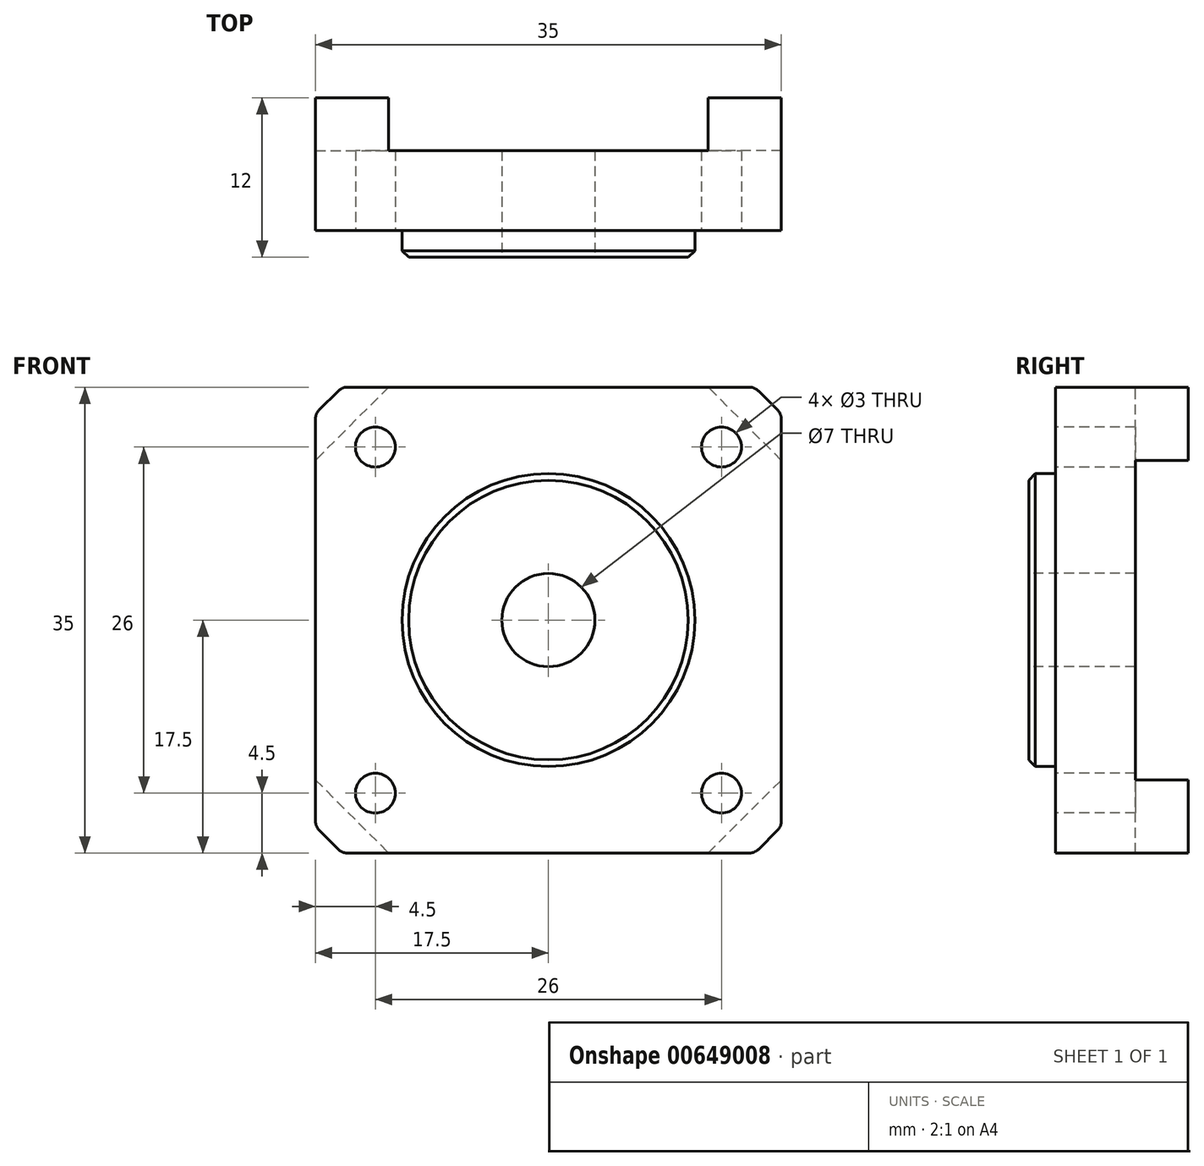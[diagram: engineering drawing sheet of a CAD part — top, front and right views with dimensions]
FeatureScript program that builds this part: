
annotation { "Feature Type Name" : "Feature", "Feature Type Description" : "" }
export const myFeature = defineFeature(function(context is Context, id is Id, definition is map)
    precondition{}
    {
        {
            var Q0;
            Q0=qCreatedBy(makeId("Front.planeOp"),FACE);
            var sketch = newSketch(context, id + "F0", { "sketchPlane" : qUnion([Q0])});
            skLineSegment(sketch, "E0.bottom", {"start": v(-17.5, 17.5) * mm, "end": v(17.5, 17.5) * mm});
            skLineSegment(sketch, "E0.top", {"start": v(-17.5, -17.5) * mm, "end": v(17.5, -17.5) * mm});
            skLineSegment(sketch, "E0.left", {"start": v(-17.5, 17.5) * mm, "end": v(-17.5, -17.5) * mm});
            skLineSegment(sketch, "E0.right", {"start": v(17.5, 17.5) * mm, "end": v(17.5, -17.5) * mm});
            skPoint(sketch, "E0.middle", {"position": v(0, 0) * mm});
            skSolve(sketch);
        }
        {
            var Q0;
            Q0=makeQuery(id+"F0.imprint","IMPRINT",FACE,{"disambiguationData":[TD([[makeQuery(id+"F0.imprint","IMPRINT",EDGE,{"derivedFrom":sQuery(id+"F0.wireOp",EDGE,"E0.bottom")}),-1.0]])]});
            extrude(context, id + "F1", {"entities" : qUnion([Q0]), "depth" : 10 * mm, "offsetDistance" : 25 * mm});
        }
        {
            var Q0;
            Q0=makeQuery(id+"F1.opExtrude","SWEPT_EDGE",EDGE,{"disambiguationData":[OSD([sQuery(id+"F0.wireOp",EDGE,"E0.bottom"),sQuery(id+"F0.wireOp",EDGE,"E0.left")])]});
            var Q1;
            Q1=makeQuery(id+"F1.opExtrude","SWEPT_EDGE",EDGE,{"disambiguationData":[OSD([sQuery(id+"F0.wireOp",EDGE,"E0.bottom"),sQuery(id+"F0.wireOp",EDGE,"E0.right")])]});
            var Q2;
            Q2=makeQuery(id+"F1.opExtrude","SWEPT_EDGE",EDGE,{"disambiguationData":[OSD([sQuery(id+"F0.wireOp",EDGE,"E0.top"),sQuery(id+"F0.wireOp",EDGE,"E0.right")])]});
            var Q3;
            Q3=makeQuery(id+"F1.opExtrude","SWEPT_EDGE",EDGE,{"disambiguationData":[OSD([sQuery(id+"F0.wireOp",EDGE,"E0.top"),sQuery(id+"F0.wireOp",EDGE,"E0.left")])]});
            chamfer(context, id + "F2", {"entities" : qUnion([Q0, Q1, Q2, Q3]), "width" : 2 * mm, "tangentPropagation" : true});
        }
        {
            var Q0;
            Q0=makeQuery(id+"F1.opExtrude","CAP_FACE",FACE,{"disambiguationData":[OSD([sQuery(id+"F0.wireOp",EDGE,"E0.bottom"),sQuery(id+"F0.wireOp",EDGE,"E0.top"),sQuery(id+"F0.wireOp",EDGE,"E0.left"),sQuery(id+"F0.wireOp",EDGE,"E0.right")])],"isStart":false});
            var sketch = newSketch(context, id + "F3", { "sketchPlane" : qUnion([Q0])});
            skCircle(sketch, "E1", {"center": v(0, 0) * mm, "radius": 11 * mm});
            skSolve(sketch);
        }
        {
            var Q0;
            Q0=makeQuery(id+"F3.imprint","IMPRINT",FACE,{"disambiguationData":[TD([[makeQuery(id+"F3.imprint","IMPRINT",EDGE,{"derivedFrom":sQuery(id+"F3.wireOp",EDGE,"E1")}),1.0]])]});
            extrude(context, id + "F4", {"entities" : qUnion([Q0]), "operationType" : NewBodyOperationType.REMOVE, "oppositeDirection" : true, "depth" : 0.5 * mm, "offsetDistance" : 25 * mm});
        }
        {
            var Q0;
            Q0=makeQuery(id+"F4.boolean.opBoolean","COPY",FACE,{"derivedFrom":makeQuery(id+"F4.opExtrude","CAP_FACE",FACE,{"disambiguationData":[OSD([sQuery(id+"F3.wireOp",EDGE,"E1")])],"isStart":false})});
            var sketch = newSketch(context, id + "F5", { "sketchPlane" : qUnion([Q0])});
            skCircle(sketch, "E2", {"center": v(0, 0) * mm, "radius": 11 * mm});
            skSolve(sketch);
        }
        {
            var Q0;
            Q0=makeQuery(id+"F5.imprint","IMPRINT",FACE,{"disambiguationData":[TD([[makeQuery(id+"F5.imprint","IMPRINT",EDGE,{"derivedFrom":sQuery(id+"F5.wireOp",EDGE,"E2")}),1.0]])]});
            extrude(context, id + "F6", {"entities" : qUnion([Q0]), "operationType" : NewBodyOperationType.ADD, "depth" : 2.5 * mm, "offsetDistance" : 25 * mm});
        }
        {
            var Q0;
            Q0=makeQuery(id+"F6.opExtrude","CAP_FACE",FACE,{"disambiguationData":[OSD([sQuery(id+"F5.wireOp",EDGE,"E2")])],"isStart":false});
            var sketch = newSketch(context, id + "F7", { "sketchPlane" : qUnion([Q0])});
            skCircle(sketch, "E3", {"center": v(0, 0) * mm, "radius": 3.5 * mm});
            skSolve(sketch);
        }
        {
            var Q0;
            Q0=makeQuery(id+"F7.imprint","IMPRINT",FACE,{"disambiguationData":[TD([[makeQuery(id+"F7.imprint","IMPRINT",EDGE,{"derivedFrom":sQuery(id+"F7.wireOp",EDGE,"E3")}),1.0]])]});
            var Q1;
            Q1=sQuery(id+"F7.wireOp",EDGE,"E3");
            extrude(context, id + "F8", {"entities" : qUnion([Q0]), "operationType" : NewBodyOperationType.REMOVE, "surfaceEntities" : qUnion([Q1]), "endBound" : BoundingType.THROUGH_ALL, "oppositeDirection" : true, "depth" : 25 * mm, "offsetDistance" : 25 * mm});
        }
        {
            var Q0;
            {var subQ0=sQuery(id+"F0.wireOp",EDGE,"E0.bottom");Q0=makeQuery(id+"F2.opChamfer","BLEND_EDGE",EDGE,{"blendedFrom":[makeQuery(id+"F1.opExtrude","SWEPT_EDGE",EDGE,{"disambiguationData":[OSD([subQ0,sQuery(id+"F0.wireOp",EDGE,"E0.left")])]}),makeQuery(id+"F1.opExtrude","SWEPT_FACE",FACE,{"disambiguationData":[OSD([subQ0])]})],"blendedInto":[makeQuery(id+"F1.opExtrude","SWEPT_FACE",FACE,{"disambiguationData":[OSD([subQ0])]})]});}
            var Q1;
            {var subQ0=sQuery(id+"F0.wireOp",EDGE,"E0.bottom");Q1=makeQuery(id+"F2.opChamfer","BLEND_EDGE",EDGE,{"blendedFrom":[makeQuery(id+"F1.opExtrude","SWEPT_EDGE",EDGE,{"disambiguationData":[OSD([subQ0,sQuery(id+"F0.wireOp",EDGE,"E0.right")])]}),makeQuery(id+"F1.opExtrude","SWEPT_FACE",FACE,{"disambiguationData":[OSD([subQ0])]})],"blendedInto":[makeQuery(id+"F1.opExtrude","SWEPT_FACE",FACE,{"disambiguationData":[OSD([subQ0])]})]});}
            var Q2;
            {var subQ0=sQuery(id+"F0.wireOp",EDGE,"E0.right");Q2=makeQuery(id+"F2.opChamfer","BLEND_EDGE",EDGE,{"blendedFrom":[makeQuery(id+"F1.opExtrude","SWEPT_EDGE",EDGE,{"disambiguationData":[OSD([sQuery(id+"F0.wireOp",EDGE,"E0.bottom"),subQ0])]}),makeQuery(id+"F1.opExtrude","SWEPT_FACE",FACE,{"disambiguationData":[OSD([subQ0])]})],"blendedInto":[makeQuery(id+"F1.opExtrude","SWEPT_FACE",FACE,{"disambiguationData":[OSD([subQ0])]})]});}
            var Q3;
            {var subQ0=sQuery(id+"F0.wireOp",EDGE,"E0.right");Q3=makeQuery(id+"F2.opChamfer","BLEND_EDGE",EDGE,{"blendedFrom":[makeQuery(id+"F1.opExtrude","SWEPT_EDGE",EDGE,{"disambiguationData":[OSD([sQuery(id+"F0.wireOp",EDGE,"E0.top"),subQ0])]}),makeQuery(id+"F1.opExtrude","SWEPT_FACE",FACE,{"disambiguationData":[OSD([subQ0])]})],"blendedInto":[makeQuery(id+"F1.opExtrude","SWEPT_FACE",FACE,{"disambiguationData":[OSD([subQ0])]})]});}
            var Q4;
            {var subQ0=sQuery(id+"F0.wireOp",EDGE,"E0.top");Q4=makeQuery(id+"F2.opChamfer","BLEND_EDGE",EDGE,{"blendedFrom":[makeQuery(id+"F1.opExtrude","SWEPT_EDGE",EDGE,{"disambiguationData":[OSD([subQ0,sQuery(id+"F0.wireOp",EDGE,"E0.right")])]}),makeQuery(id+"F1.opExtrude","SWEPT_FACE",FACE,{"disambiguationData":[OSD([subQ0])]})],"blendedInto":[makeQuery(id+"F1.opExtrude","SWEPT_FACE",FACE,{"disambiguationData":[OSD([subQ0])]})]});}
            var Q5;
            {var subQ0=sQuery(id+"F0.wireOp",EDGE,"E0.top");Q5=makeQuery(id+"F2.opChamfer","BLEND_EDGE",EDGE,{"blendedFrom":[makeQuery(id+"F1.opExtrude","SWEPT_EDGE",EDGE,{"disambiguationData":[OSD([subQ0,sQuery(id+"F0.wireOp",EDGE,"E0.left")])]}),makeQuery(id+"F1.opExtrude","SWEPT_FACE",FACE,{"disambiguationData":[OSD([subQ0])]})],"blendedInto":[makeQuery(id+"F1.opExtrude","SWEPT_FACE",FACE,{"disambiguationData":[OSD([subQ0])]})]});}
            var Q6;
            {var subQ0=sQuery(id+"F0.wireOp",EDGE,"E0.left");Q6=makeQuery(id+"F2.opChamfer","BLEND_EDGE",EDGE,{"blendedFrom":[makeQuery(id+"F1.opExtrude","SWEPT_EDGE",EDGE,{"disambiguationData":[OSD([sQuery(id+"F0.wireOp",EDGE,"E0.top"),subQ0])]}),makeQuery(id+"F1.opExtrude","SWEPT_FACE",FACE,{"disambiguationData":[OSD([subQ0])]})],"blendedInto":[makeQuery(id+"F1.opExtrude","SWEPT_FACE",FACE,{"disambiguationData":[OSD([subQ0])]})]});}
            var Q7;
            {var subQ0=sQuery(id+"F0.wireOp",EDGE,"E0.left");Q7=makeQuery(id+"F2.opChamfer","BLEND_EDGE",EDGE,{"blendedFrom":[makeQuery(id+"F1.opExtrude","SWEPT_EDGE",EDGE,{"disambiguationData":[OSD([sQuery(id+"F0.wireOp",EDGE,"E0.bottom"),subQ0])]}),makeQuery(id+"F1.opExtrude","SWEPT_FACE",FACE,{"disambiguationData":[OSD([subQ0])]})],"blendedInto":[makeQuery(id+"F1.opExtrude","SWEPT_FACE",FACE,{"disambiguationData":[OSD([subQ0])]})]});}
            fillet(context, id + "F9", {"entities" : qUnion([Q0, Q1, Q2, Q3, Q4, Q5, Q6, Q7]), "radius" : 1 * mm, "tangentPropagation" : true, "allowEdgeOverflow" : false});
        }
        {
            var Q0;
            Q0=makeQuery(id+"F6.opExtrude","CAP_EDGE",EDGE,{"disambiguationData":[OSD([sQuery(id+"F5.wireOp",EDGE,"E2")])],"isStart":false});
            var Q1;
            Q1=makeQuery(id+"F8.boolean.opBoolean","COPY",EDGE,{"derivedFrom":makeQuery(id+"F8.opExtrude","CAP_EDGE",EDGE,{"disambiguationData":[OSD([sQuery(id+"F7.wireOp",EDGE,"E3")])],"isStart":true})});
            var Q2;
            Q2=makeQuery(id+"F6.opExtrude","CAP_EDGE",EDGE,{"disambiguationData":[OSD([sQuery(id+"F5.wireOp",EDGE,"E2")])],"isStart":true});
            chamfer(context, id + "F10", {"entities" : qUnion([Q0, Q1, Q2]), "width" : 0.5 * mm, "tangentPropagation" : true});
        }
        {
            var Q0;
            Q0=makeQuery(id+"F1.opExtrude","CAP_FACE",FACE,{"disambiguationData":[OSD([sQuery(id+"F0.wireOp",EDGE,"E0.bottom"),sQuery(id+"F0.wireOp",EDGE,"E0.top"),sQuery(id+"F0.wireOp",EDGE,"E0.left"),sQuery(id+"F0.wireOp",EDGE,"E0.right")])],"isStart":false});
            var sketch = newSketch(context, id + "F11", { "sketchPlane" : qUnion([Q0])});
            skCircle(sketch, "E4", {"center": v(-13, 13) * mm, "radius": 1.5 * mm});
            skCircle(sketch, "E5.1.0", {"center": v(-13, -13) * mm, "radius": 1.5 * mm});
            skCircle(sketch, "E5.2.0", {"center": v(13, -13) * mm, "radius": 1.5 * mm});
            skCircle(sketch, "E5.3.0", {"center": v(13, 13) * mm, "radius": 1.5 * mm});
            skPoint(sketch, "E5.center", {"position": v(0, 0) * mm});
            skSolve(sketch);
        }
        {
            var Q0;
            Q0=qSketchRegion(id+"F11",true);
            extrude(context, id + "F12", {"entities" : qUnion([Q0]), "operationType" : NewBodyOperationType.REMOVE, "endBound" : BoundingType.THROUGH_ALL, "oppositeDirection" : true, "depth" : 25 * mm, "offsetDistance" : 25 * mm});
        }
        {
            var Q0;
            Q0=makeQuery(id+"F1.opExtrude","CAP_FACE",FACE,{"disambiguationData":[OSD([sQuery(id+"F0.wireOp",EDGE,"E0.bottom"),sQuery(id+"F0.wireOp",EDGE,"E0.top"),sQuery(id+"F0.wireOp",EDGE,"E0.left"),sQuery(id+"F0.wireOp",EDGE,"E0.right")])],"isStart":true});
            var sketch = newSketch(context, id + "F13", { "sketchPlane" : qUnion([Q0])});
            skLineSegment(sketch, "E6.bottom", {"start": v(-12, 17.5) * mm, "end": v(12, 17.5) * mm});
            skLineSegment(sketch, "E6.top", {"start": v(-12, -17.5) * mm, "end": v(12, -17.5) * mm});
            skLineSegment(sketch, "E6.left", {"start": v(-17.5, 12) * mm, "end": v(-17.5, -12) * mm});
            skLineSegment(sketch, "E6.right", {"start": v(17.5, 12) * mm, "end": v(17.5, -12) * mm});
            skPoint(sketch, "E6.middle", {"position": v(0, 0) * mm});
            skLineSegment(sketch, "E7", {"start": v(-17.5, 12) * mm, "end": v(-12, 17.5) * mm});
            skLineSegment(sketch, "E8.1.0", {"start": v(-12, -17.5) * mm, "end": v(-17.5, -12) * mm});
            skLineSegment(sketch, "E8.2.0", {"start": v(17.5, -12) * mm, "end": v(12, -17.5) * mm});
            skLineSegment(sketch, "E8.3.0", {"start": v(12, 17.5) * mm, "end": v(17.5, 12) * mm});
            skPoint(sketch, "E9.orphan", {"position": v(-17.5, 17.5) * mm});
            skPoint(sketch, "E10.orphan", {"position": v(-17.5, -17.5) * mm});
            skPoint(sketch, "E11.orphan", {"position": v(17.5, -17.5) * mm});
            skPoint(sketch, "E12.orphan", {"position": v(17.5, 17.5) * mm});
            skSolve(sketch);
        }
        {
            var Q0;
            Q0=qSketchRegion(id+"F13",true);
            extrude(context, id + "F14", {"entities" : qUnion([Q0]), "operationType" : NewBodyOperationType.REMOVE, "oppositeDirection" : true, "depth" : 4 * mm, "offsetDistance" : 25 * mm});
        }
    });
